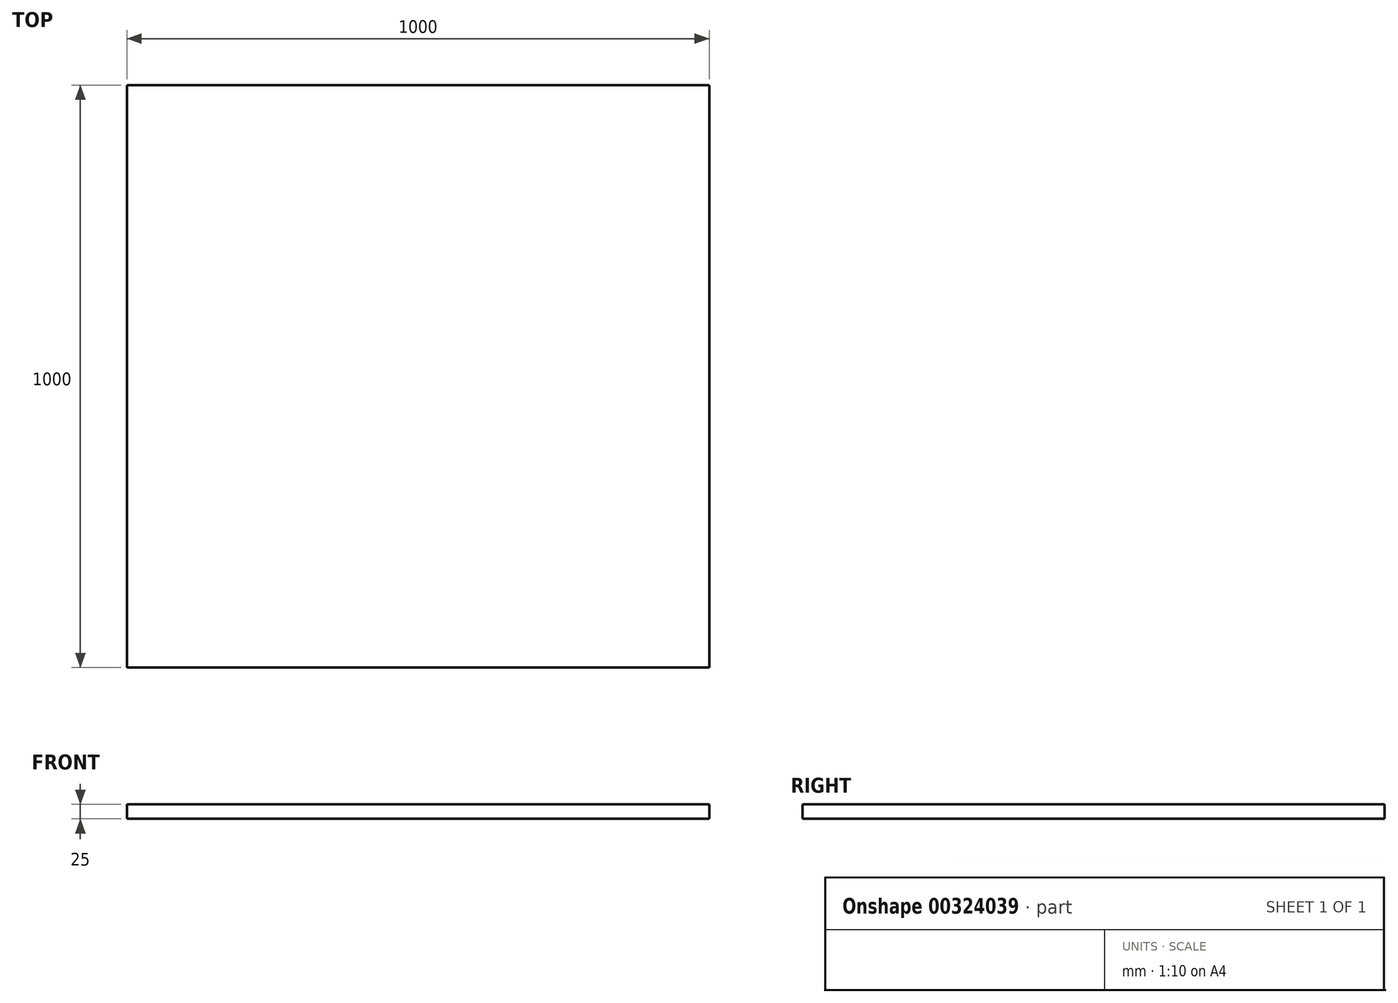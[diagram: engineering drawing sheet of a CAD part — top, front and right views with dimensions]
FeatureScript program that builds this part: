
annotation { "Feature Type Name" : "Feature", "Feature Type Description" : "" }
export const myFeature = defineFeature(function(context is Context, id is Id, definition is map)
    precondition{}
    {
        {
            var Q0;
            Q0=qCreatedBy(makeId("Top.planeOp"),FACE);
            var sketch = newSketch(context, id + "F0", { "sketchPlane" : qUnion([Q0])});
            skLineSegment(sketch, "E0.bottom", {"start": v(500, -500) * mm, "end": v(-500, -500) * mm});
            skLineSegment(sketch, "E0.top", {"start": v(500, 500) * mm, "end": v(-500, 500) * mm});
            skLineSegment(sketch, "E0.left", {"start": v(500, -500) * mm, "end": v(500, 500) * mm});
            skLineSegment(sketch, "E0.right", {"start": v(-500, -500) * mm, "end": v(-500, 500) * mm});
            skPoint(sketch, "E0.middle", {"position": v(0, 0) * mm});
            skSolve(sketch);
        }
        {
            var Q0;
            Q0=makeQuery(id+"F0.imprint","IMPRINT",FACE,{"disambiguationData":[TD([[makeQuery(id+"F0.imprint","IMPRINT",EDGE,{"derivedFrom":sQuery(id+"F0.wireOp",EDGE,"E0.bottom")}),-1.0]])]});
            extrude(context, id + "F1", {"entities" : qUnion([Q0]), "depth" : 25 * mm});
        }
    });
